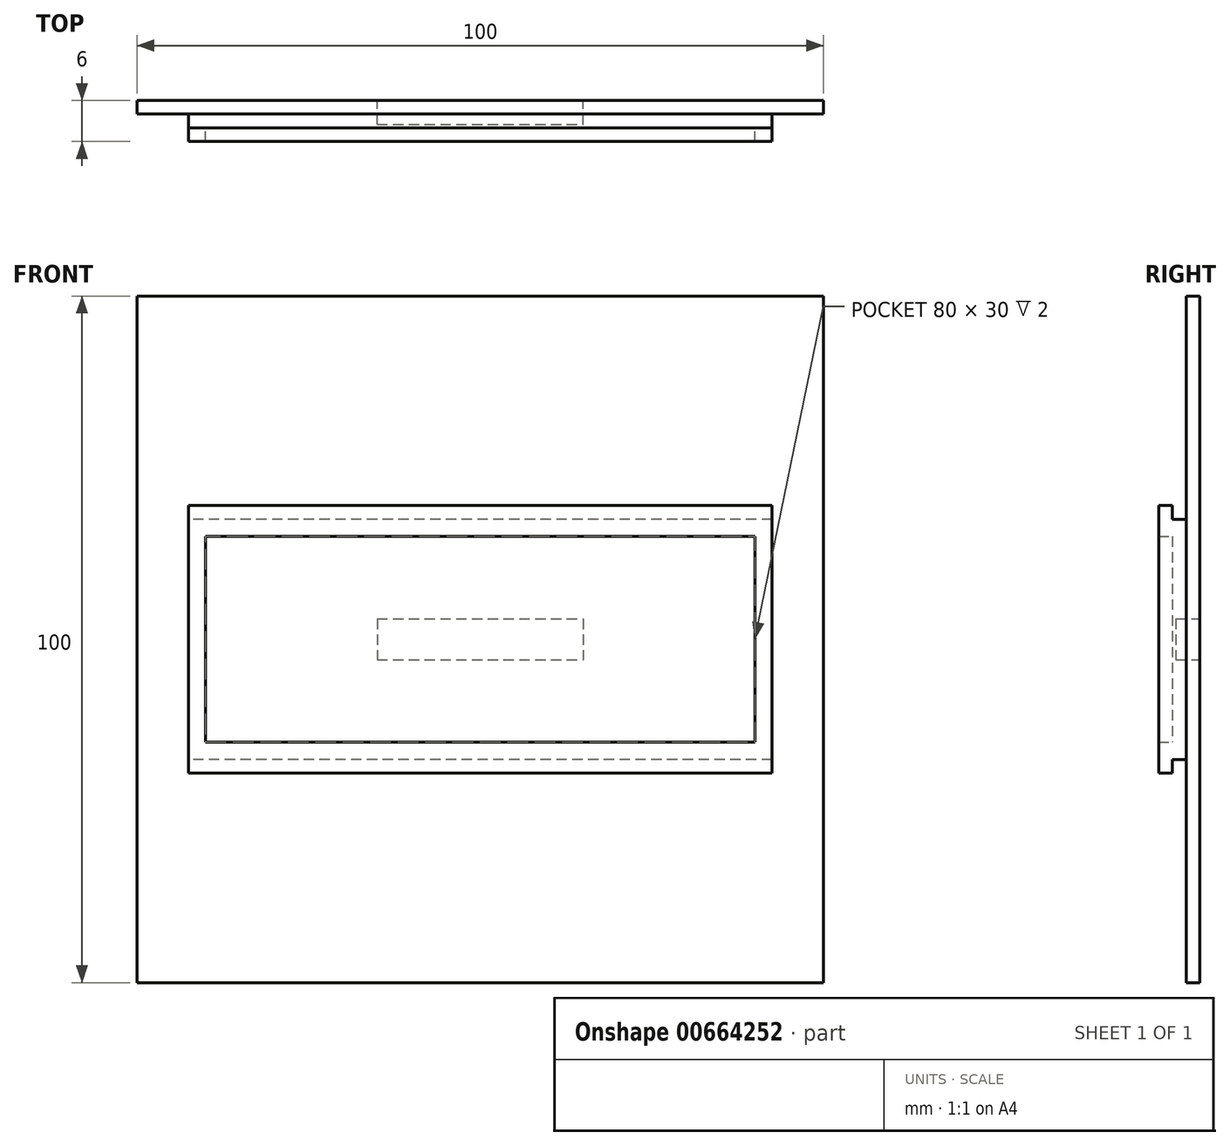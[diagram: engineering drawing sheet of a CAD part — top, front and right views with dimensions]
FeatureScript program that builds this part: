
annotation { "Feature Type Name" : "Feature", "Feature Type Description" : "" }
export const myFeature = defineFeature(function(context is Context, id is Id, definition is map)
    precondition{}
    {
        {
            var Q0;
            Q0=qCreatedBy(makeId("Front.planeOp"),FACE);
            var sketch = newSketch(context, id + "F0", { "sketchPlane" : qUnion([Q0])});
            skLineSegment(sketch, "E0.bottom", {"start": v(40, 15) * mm, "end": v(-40, 15) * mm});
            skLineSegment(sketch, "E0.top", {"start": v(40, -15) * mm, "end": v(-40, -15) * mm});
            skLineSegment(sketch, "E0.left", {"start": v(40, 15) * mm, "end": v(40, -15) * mm});
            skLineSegment(sketch, "E0.right", {"start": v(-40, 15) * mm, "end": v(-40, -15) * mm});
            skPoint(sketch, "E0.middle", {"position": v(0, 0) * mm});
            skLineSegment(sketch, "E1.bottom", {"start": v(42.5, 17.5) * mm, "end": v(-42.5, 17.5) * mm});
            skLineSegment(sketch, "E1.top", {"start": v(42.5, -17.5) * mm, "end": v(-42.5, -17.5) * mm});
            skLineSegment(sketch, "E1.left", {"start": v(42.5, 17.5) * mm, "end": v(42.5, -17.5) * mm});
            skLineSegment(sketch, "E1.right", {"start": v(-42.5, 17.5) * mm, "end": v(-42.5, -17.5) * mm});
            skLineSegment(sketch, "E2.bottom", {"start": v(50, 50) * mm, "end": v(-50, 50) * mm});
            skLineSegment(sketch, "E2.top", {"start": v(50, -50) * mm, "end": v(-50, -50) * mm});
            skLineSegment(sketch, "E2.left", {"start": v(50, 50) * mm, "end": v(50, -50) * mm});
            skLineSegment(sketch, "E2.right", {"start": v(-50, 50) * mm, "end": v(-50, -50) * mm});
            skSolve(sketch);
        }
        {
            var Q0;
            Q0=makeQuery(id+"F0.imprint","IMPRINT",FACE,{"disambiguationData":[TD([[makeQuery(id+"F0.imprint","IMPRINT",EDGE,{"derivedFrom":sQuery(id+"F0.wireOp",EDGE,"E0.bottom")}),1.0]])]});
            var Q1;
            Q1=makeQuery(id+"F0.imprint","IMPRINT",FACE,{"disambiguationData":[TD([[makeQuery(id+"F0.imprint","IMPRINT",EDGE,{"derivedFrom":sQuery(id+"F0.wireOp",EDGE,"E0.bottom")}),-1.0]])]});
            var Q2;
            Q2=makeQuery(id+"F0.imprint","IMPRINT",FACE,{"disambiguationData":[TD([[makeQuery(id+"F0.imprint","IMPRINT",EDGE,{"derivedFrom":sQuery(id+"F0.wireOp",EDGE,"E1.bottom")}),-1.0]])]});
            extrude(context, id + "F1", {"entities" : qUnion([Q0, Q1, Q2]), "oppositeDirection" : true, "depth" : 2 * mm, "offsetDistance" : 25 * mm});
        }
        {
            var Q0;
            Q0=makeQuery(id+"F0.imprint","IMPRINT",FACE,{"disambiguationData":[TD([[makeQuery(id+"F0.imprint","IMPRINT",EDGE,{"derivedFrom":sQuery(id+"F0.wireOp",EDGE,"E0.bottom")}),-1.0]])]});
            extrude(context, id + "F2", {"entities" : qUnion([Q0]), "operationType" : NewBodyOperationType.ADD, "depth" : 4 * mm, "offsetDistance" : 25 * mm});
        }
        {
            var Q0;
            Q0=makeQuery(id+"F2.opExtrude","SWEPT_FACE",FACE,{"disambiguationData":[OSD([sQuery(id+"F0.wireOp",EDGE,"E1.top")])]});
            var sketch = newSketch(context, id + "F3", { "sketchPlane" : qUnion([Q0])});
            skLineSegment(sketch, "E3.bottom", {"start": v(-42.5, 4) * mm, "end": v(42.5, 4) * mm});
            skLineSegment(sketch, "E3.top", {"start": v(-42.5, 2) * mm, "end": v(42.5, 2) * mm});
            skLineSegment(sketch, "E3.left", {"start": v(-42.5, 4) * mm, "end": v(-42.5, 2) * mm});
            skLineSegment(sketch, "E3.right", {"start": v(42.5, 4) * mm, "end": v(42.5, 2) * mm});
            skSolve(sketch);
        }
        {
            var Q0;
            Q0=makeQuery(id+"F3.imprint","IMPRINT",FACE,{"disambiguationData":[TD([[makeQuery(id+"F3.imprint","IMPRINT",EDGE,{"derivedFrom":sQuery(id+"F3.wireOp",EDGE,"E3.bottom")}),1.0]])]});
            extrude(context, id + "F4", {"entities" : qUnion([Q0]), "operationType" : NewBodyOperationType.ADD, "depth" : 2 * mm, "offsetDistance" : 25 * mm});
        }
        {
            var Q0;
            Q0=makeQuery(id+"F2.opExtrude","SWEPT_FACE",FACE,{"disambiguationData":[OSD([sQuery(id+"F0.wireOp",EDGE,"E1.bottom")])]});
            var sketch = newSketch(context, id + "F5", { "sketchPlane" : qUnion([Q0])});
            skLineSegment(sketch, "E4.bottom", {"start": v(42.5, -4) * mm, "end": v(-42.5, -4) * mm});
            skLineSegment(sketch, "E4.top", {"start": v(42.5, -2) * mm, "end": v(-42.5, -2) * mm});
            skLineSegment(sketch, "E4.left", {"start": v(42.5, -4) * mm, "end": v(42.5, -2) * mm});
            skLineSegment(sketch, "E4.right", {"start": v(-42.5, -4) * mm, "end": v(-42.5, -2) * mm});
            skSolve(sketch);
        }
        {
            var Q0;
            Q0=makeQuery(id+"F5.imprint","IMPRINT",FACE,{"disambiguationData":[TD([[makeQuery(id+"F5.imprint","IMPRINT",EDGE,{"derivedFrom":sQuery(id+"F5.wireOp",EDGE,"E4.bottom")}),-1.0]])]});
            extrude(context, id + "F6", {"entities" : qUnion([Q0]), "operationType" : NewBodyOperationType.ADD, "depth" : 2 * mm, "offsetDistance" : 25 * mm});
        }
        {
            var Q0;
            Q0=makeQuery(id+"F0.imprint","IMPRINT",FACE,{"disambiguationData":[TD([[makeQuery(id+"F0.imprint","IMPRINT",EDGE,{"derivedFrom":sQuery(id+"F0.wireOp",EDGE,"E0.bottom")}),1.0]])]});
            extrude(context, id + "F7", {"entities" : qUnion([Q0]), "operationType" : NewBodyOperationType.ADD, "depth" : 2 * mm, "offsetDistance" : 25 * mm});
        }
        {
            var Q0;
            Q0=makeQuery(id+"F1.opExtrude","CAP_FACE",FACE,{"disambiguationData":[OSD([sQuery(id+"F0.wireOp",EDGE,"E2.bottom"),sQuery(id+"F0.wireOp",EDGE,"E2.top"),sQuery(id+"F0.wireOp",EDGE,"E2.left"),sQuery(id+"F0.wireOp",EDGE,"E2.right")])],"isStart":false});
            var sketch = newSketch(context, id + "F8", { "sketchPlane" : qUnion([Q0])});
            skLineSegment(sketch, "E5.bottom", {"start": v(15, 3) * mm, "end": v(-15, 3) * mm});
            skLineSegment(sketch, "E5.top", {"start": v(15, -3) * mm, "end": v(-15, -3) * mm});
            skLineSegment(sketch, "E5.left", {"start": v(15, 3) * mm, "end": v(15, -3) * mm});
            skLineSegment(sketch, "E5.right", {"start": v(-15, 3) * mm, "end": v(-15, -3) * mm});
            skPoint(sketch, "E5.middle", {"position": v(0, 0) * mm});
            skSolve(sketch);
        }
        {
            var Q0;
            Q0=makeQuery(id+"F8.imprint","IMPRINT",FACE,{"disambiguationData":[TD([[makeQuery(id+"F8.imprint","IMPRINT",EDGE,{"derivedFrom":sQuery(id+"F8.wireOp",EDGE,"E5.bottom")}),1.0]])]});
            extrude(context, id + "F9", {"entities" : qUnion([Q0]), "operationType" : NewBodyOperationType.REMOVE, "oppositeDirection" : true, "depth" : 3.5 * mm, "offsetDistance" : 25 * mm});
        }
    });
